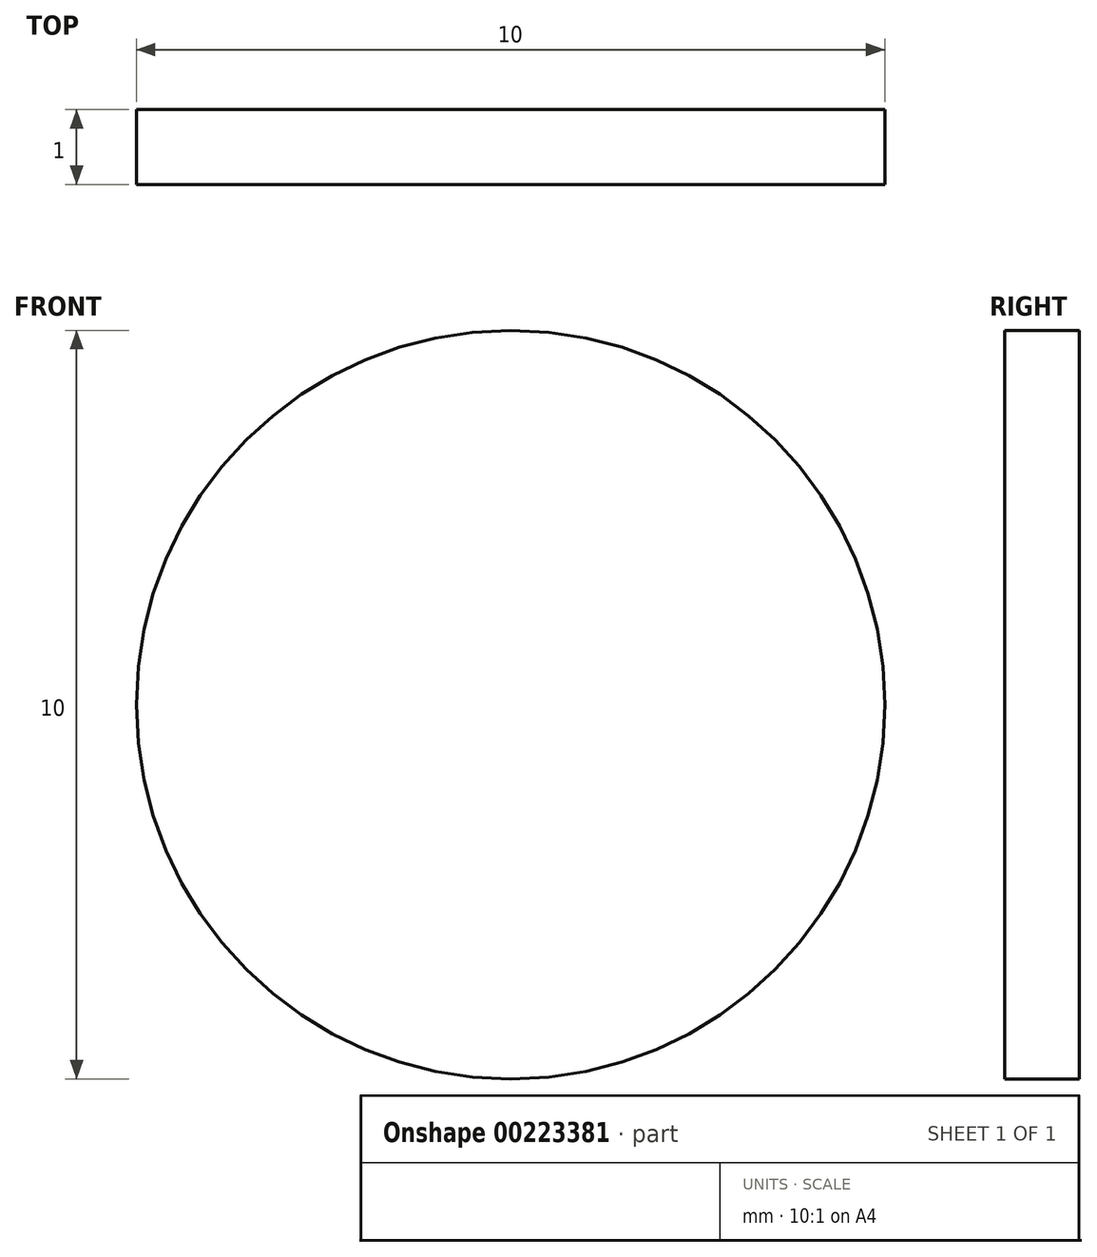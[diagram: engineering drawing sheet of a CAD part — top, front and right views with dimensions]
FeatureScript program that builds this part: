
annotation { "Feature Type Name" : "Feature", "Feature Type Description" : "" }
export const myFeature = defineFeature(function(context is Context, id is Id, definition is map)
    precondition{}
    {
        {
            var Q0;
            Q0=qCreatedBy(makeId("Front.planeOp"),FACE);
            var sketch = newSketch(context, id + "F0", { "sketchPlane" : qUnion([Q0])});
            skCircle(sketch, "E0", {"center": v(0, 0) * mm, "radius": 5 * mm});
            skSolve(sketch);
        }
        {
            var Q0;
            Q0 = qSketchRegion(id + "F0", true);
            extrude(context, id + "F1", {"entities" : qUnion([Q0]), "depth" : 1 * mm});
        }
    });
